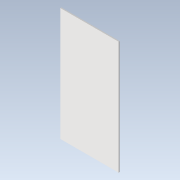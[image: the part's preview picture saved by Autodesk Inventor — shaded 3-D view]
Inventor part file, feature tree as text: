
AUTODESK INVENTOR PART (.ipt)
format: ipt  version: 2021 (Build 250183000, 183)  size: 73,216 bytes
history: native  units: mm
features: other x1, extrude x1, sketch x1
ambient origin geometry x8: Origin, YZ Plane, XZ Plane, XY Plane, X Axis, Y Axis, Z Axis, Center Point
bodies: Body1 (feature_tree)
feature tree (3):
  other  "Sólido1"
  extrude  "Extrusión1"  [1 undecoded]
  sketch  "Boceto1"  dims[d0=1.0mm d1=0.0mm]
note: 1 required parameter value undecoded (feature->parameter linkage not recoverable at this tier; creation-order binding heuristic only, values carry confidence <= 0.55)
